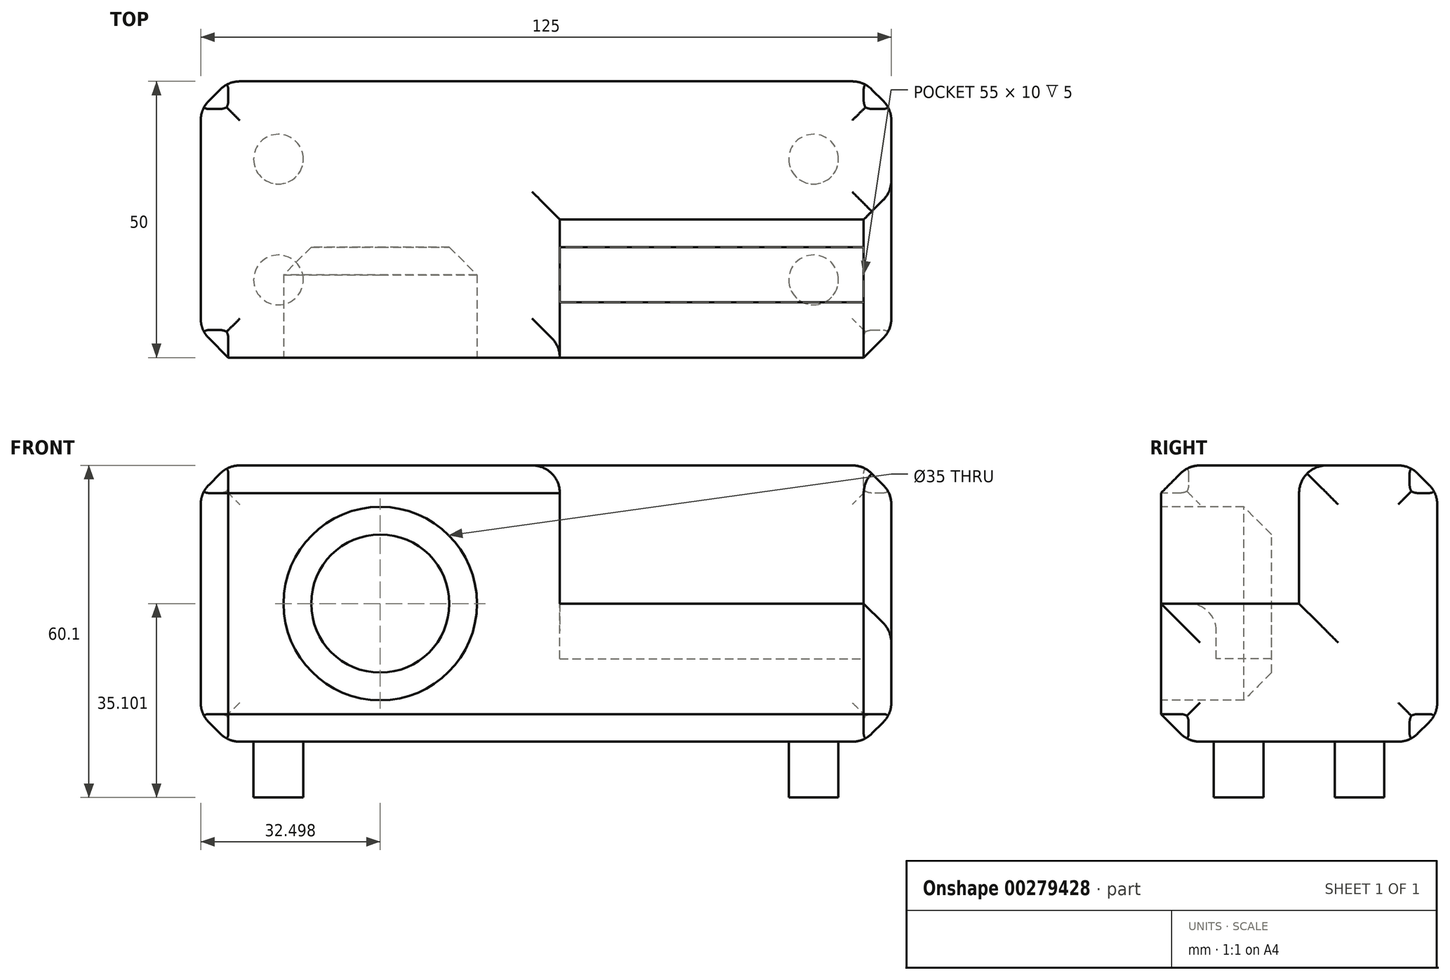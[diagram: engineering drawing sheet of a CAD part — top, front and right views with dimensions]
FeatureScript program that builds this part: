
annotation { "Feature Type Name" : "Feature", "Feature Type Description" : "" }
export const myFeature = defineFeature(function(context is Context, id is Id, definition is map)
    precondition{}
    {
        {
            var Q0;
            Q0=qCreatedBy(makeId("Front.planeOp"),FACE);
            var sketch = newSketch(context, id + "F0", { "sketchPlane" : qUnion([Q0])});
            skLineSegment(sketch, "E0.bottom", {"start": v(-58.26, 27.77) * mm, "end": v(66.74, 27.77) * mm});
            skLineSegment(sketch, "E0.top", {"start": v(-58.26, -22.23) * mm, "end": v(66.74, -22.23) * mm});
            skLineSegment(sketch, "E0.left", {"start": v(-58.26, 27.77) * mm, "end": v(-58.26, -22.23) * mm});
            skLineSegment(sketch, "E0.right", {"start": v(66.74, 27.77) * mm, "end": v(66.74, -22.23) * mm});
            skSolve(sketch);
        }
        {
            var Q0;
            Q0=makeQuery(id+"F0.imprint","IMPRINT",FACE,{"disambiguationData":[TD([[makeQuery(id+"F0.imprint","IMPRINT",EDGE,{"derivedFrom":sQuery(id+"F0.wireOp",EDGE,"E0.bottom")}),-1.0]])]});
            extrude(context, id + "F1", {"entities" : qUnion([Q0]), "depth" : 50 * mm});
        }
        {
            var Q0;
            Q0=makeQuery(id+"F1.opExtrude","CAP_FACE",FACE,{"disambiguationData":[OSD([sQuery(id+"F0.wireOp",EDGE,"E0.bottom"),sQuery(id+"F0.wireOp",EDGE,"E0.top"),sQuery(id+"F0.wireOp",EDGE,"E0.left"),sQuery(id+"F0.wireOp",EDGE,"E0.right")])],"isStart":false});
            var sketch = newSketch(context, id + "F2", { "sketchPlane" : qUnion([Q0])});
            skLineSegment(sketch, "E1.bottom", {"start": v(6.74, 27.77) * mm, "end": v(66.74, 27.77) * mm});
            skLineSegment(sketch, "E1.top", {"start": v(6.74, 2.77) * mm, "end": v(66.74, 2.77) * mm});
            skLineSegment(sketch, "E1.left", {"start": v(6.74, 27.77) * mm, "end": v(6.74, 2.77) * mm});
            skLineSegment(sketch, "E1.right", {"start": v(66.74, 27.77) * mm, "end": v(66.74, 2.77) * mm});
            skSolve(sketch);
        }
        {
            var Q0;
            Q0=qSketchRegion(id+"F2",true);
            extrude(context, id + "F3", {"entities" : qUnion([Q0]), "operationType" : NewBodyOperationType.REMOVE, "oppositeDirection" : true, "depth" : 25 * mm});
        }
        {
            var Q0;
            Q0=makeQuery(id+"F1.opExtrude","CAP_FACE",FACE,{"disambiguationData":[OSD([sQuery(id+"F0.wireOp",EDGE,"E0.bottom"),sQuery(id+"F0.wireOp",EDGE,"E0.top"),sQuery(id+"F0.wireOp",EDGE,"E0.left"),sQuery(id+"F0.wireOp",EDGE,"E0.right")])],"isStart":false});
            var sketch = newSketch(context, id + "F4", { "sketchPlane" : qUnion([Q0])});
            skCircle(sketch, "E2", {"center": v(-25.76, 2.77) * mm, "radius": 17.5 * mm});
            skSolve(sketch);
        }
        {
            var Q0;
            Q0=qSketchRegion(id+"F4",true);
            extrude(context, id + "F5", {"entities" : qUnion([Q0]), "operationType" : NewBodyOperationType.REMOVE, "oppositeDirection" : true, "depth" : 20 * mm});
        }
        {
            var Q0;
            Q0=makeQuery(id+"F1.opExtrude","CAP_EDGE",EDGE,{"disambiguationData":[OSD([sQuery(id+"F0.wireOp",EDGE,"E0.bottom")])],"isStart":false});
            var Q1;
            Q1=makeQuery(id+"F3.boolean.opBoolean","COPY",EDGE,{"derivedFrom":makeQuery(id+"F3.opExtrude","SWEPT_EDGE",EDGE,{"disambiguationData":[OSD([sQuery(id+"F0.wireOp",EDGE,"E0.bottom"),sQuery(id+"F2.wireOp",EDGE,"E1.bottom"),sQuery(id+"F2.wireOp",EDGE,"E1.left")])]})});
            var Q2;
            Q2=makeQuery(id+"F3.boolean.opBoolean","COPY",EDGE,{"derivedFrom":makeQuery(id+"F3.opExtrude","CAP_EDGE",EDGE,{"disambiguationData":[OSD([sQuery(id+"F2.wireOp",EDGE,"E1.bottom")])],"isStart":false})});
            var Q3;
            Q3=makeQuery(id+"F1.opExtrude","SWEPT_EDGE",EDGE,{"disambiguationData":[OSD([sQuery(id+"F0.wireOp",EDGE,"E0.bottom"),sQuery(id+"F0.wireOp",EDGE,"E0.right")])]});
            var Q4;
            Q4=makeQuery(id+"F1.opExtrude","CAP_EDGE",EDGE,{"disambiguationData":[OSD([sQuery(id+"F0.wireOp",EDGE,"E0.bottom")])],"isStart":true});
            var Q5;
            Q5=makeQuery(id+"F1.opExtrude","SWEPT_EDGE",EDGE,{"disambiguationData":[OSD([sQuery(id+"F0.wireOp",EDGE,"E0.bottom"),sQuery(id+"F0.wireOp",EDGE,"E0.left")])]});
            var Q6;
            Q6=makeQuery(id+"F1.opExtrude","CAP_EDGE",EDGE,{"disambiguationData":[OSD([sQuery(id+"F0.wireOp",EDGE,"E0.left")])],"isStart":false});
            var Q7;
            Q7=makeQuery(id+"F5.boolean.opBoolean","COPY",EDGE,{"derivedFrom":makeQuery(id+"F5.opExtrude","CAP_EDGE",EDGE,{"disambiguationData":[OSD([sQuery(id+"F4.wireOp",EDGE,"E2")])],"isStart":true})});
            var Q8;
            Q8=makeQuery(id+"F5.boolean.opBoolean","COPY",EDGE,{"derivedFrom":makeQuery(id+"F5.opExtrude","CAP_EDGE",EDGE,{"disambiguationData":[OSD([sQuery(id+"F4.wireOp",EDGE,"E2")])],"isStart":false})});
            var Q9;
            Q9=makeQuery(id+"F3.boolean.opBoolean","COPY",EDGE,{"derivedFrom":makeQuery(id+"F3.opExtrude","CAP_EDGE",EDGE,{"disambiguationData":[OSD([sQuery(id+"F2.wireOp",EDGE,"E1.top")])],"isStart":true})});
            var Q10;
            Q10=makeQuery(id+"F3.boolean.opBoolean","COPY",EDGE,{"derivedFrom":makeQuery(id+"F3.opExtrude","CAP_EDGE",EDGE,{"disambiguationData":[OSD([sQuery(id+"F2.wireOp",EDGE,"E1.left")])],"isStart":true})});
            var Q11;
            Q11=makeQuery(id+"F3.boolean.opBoolean","COPY",EDGE,{"derivedFrom":makeQuery(id+"F3.opExtrude","CAP_EDGE",EDGE,{"disambiguationData":[OSD([sQuery(id+"F2.wireOp",EDGE,"E1.right")])],"isStart":false})});
            var Q12;
            Q12=makeQuery(id+"F3.boolean.opBoolean","COPY",EDGE,{"derivedFrom":makeQuery(id+"F3.opExtrude","SWEPT_EDGE",EDGE,{"disambiguationData":[OSD([sQuery(id+"F0.wireOp",EDGE,"E0.right"),sQuery(id+"F2.wireOp",EDGE,"E1.top"),sQuery(id+"F2.wireOp",EDGE,"E1.right")])]})});
            var Q13;
            Q13=makeQuery(id+"F1.opExtrude","SWEPT_EDGE",EDGE,{"disambiguationData":[OSD([sQuery(id+"F0.wireOp",EDGE,"E0.top"),sQuery(id+"F0.wireOp",EDGE,"E0.right")])]});
            var Q14;
            Q14=makeQuery(id+"F1.opExtrude","SWEPT_FACE",FACE,{"disambiguationData":[OSD([sQuery(id+"F0.wireOp",EDGE,"E0.right")])]});
            var Q15;
            Q15=makeQuery(id+"F1.opExtrude","CAP_EDGE",EDGE,{"disambiguationData":[OSD([sQuery(id+"F0.wireOp",EDGE,"E0.top")])],"isStart":false});
            var Q16;
            Q16=makeQuery(id+"F1.opExtrude","CAP_EDGE",EDGE,{"disambiguationData":[OSD([sQuery(id+"F0.wireOp",EDGE,"E0.left")])],"isStart":true});
            var Q17;
            Q17=makeQuery(id+"F1.opExtrude","CAP_EDGE",EDGE,{"disambiguationData":[OSD([sQuery(id+"F0.wireOp",EDGE,"E0.top")])],"isStart":true});
            var Q18;
            Q18=makeQuery(id+"F1.opExtrude","SWEPT_EDGE",EDGE,{"disambiguationData":[OSD([sQuery(id+"F0.wireOp",EDGE,"E0.top"),sQuery(id+"F0.wireOp",EDGE,"E0.left")])]});
            chamfer(context, id + "F6", {"entities" : qUnion([Q0, Q1, Q2, Q3, Q4, Q5, Q6, Q7, Q8, Q9, Q10, Q11, Q12, Q13, Q14, Q15, Q16, Q17, Q18]), "width" : 5 * mm, "tangentPropagation" : true});
        }
        {
            var Q0;
            Q0=makeQuery(id+"F3.boolean.opBoolean","COPY",FACE,{"derivedFrom":makeQuery(id+"F3.opExtrude","SWEPT_FACE",FACE,{"disambiguationData":[OSD([sQuery(id+"F2.wireOp",EDGE,"E1.top")])]})});
            var sketch = newSketch(context, id + "F7", { "sketchPlane" : qUnion([Q0])});
            skLineSegment(sketch, "E3.bottom", {"start": v(6.74, -40) * mm, "end": v(61.74, -40) * mm});
            skLineSegment(sketch, "E3.top", {"start": v(6.74, -30) * mm, "end": v(61.74, -30) * mm});
            skLineSegment(sketch, "E3.left", {"start": v(6.74, -40) * mm, "end": v(6.74, -30) * mm});
            skLineSegment(sketch, "E3.right", {"start": v(61.74, -40) * mm, "end": v(61.74, -30) * mm});
            skSolve(sketch);
        }
        {
            var Q0;
            Q0=makeQuery(id+"F7.imprint","IMPRINT",FACE,{"disambiguationData":[TD([[makeQuery(id+"F7.imprint","IMPRINT",EDGE,{"derivedFrom":sQuery(id+"F7.wireOp",EDGE,"E3.bottom")}),1.0]])]});
            extrude(context, id + "F8", {"entities" : qUnion([Q0]), "operationType" : NewBodyOperationType.REMOVE, "oppositeDirection" : true, "depth" : 10 * mm});
        }
        {
            var Q0;
            Q0=makeQuery(id+"F1.opExtrude","SWEPT_FACE",FACE,{"disambiguationData":[OSD([sQuery(id+"F0.wireOp",EDGE,"E0.bottom")])]});
            var Q1;
            Q1=makeQuery(id+"F1.opExtrude","SWEPT_FACE",FACE,{"disambiguationData":[OSD([sQuery(id+"F0.wireOp",EDGE,"E0.top")])]});
            var Q2;
            Q2=makeQuery(id+"F1.opExtrude","CAP_FACE",FACE,{"disambiguationData":[OSD([sQuery(id+"F0.wireOp",EDGE,"E0.bottom"),sQuery(id+"F0.wireOp",EDGE,"E0.top"),sQuery(id+"F0.wireOp",EDGE,"E0.left"),sQuery(id+"F0.wireOp",EDGE,"E0.right")])],"isStart":true});
            var Q3;
            Q3=makeQuery(id+"F1.opExtrude","SWEPT_FACE",FACE,{"disambiguationData":[OSD([sQuery(id+"F0.wireOp",EDGE,"E0.right")])]});
            var Q4;
            Q4=makeQuery(id+"F1.opExtrude","SWEPT_FACE",FACE,{"disambiguationData":[OSD([sQuery(id+"F0.wireOp",EDGE,"E0.left")])]});
            fillet(context, id + "F9", {"entities" : qUnion([Q0, Q1, Q2, Q3, Q4]), "radius" : 5 * mm, "tangentPropagation" : true, "allowEdgeOverflow" : false});
        }
        {
            var Q0;
            Q0=makeQuery(id+"F8.boolean.opBoolean","COPY",EDGE,{"derivedFrom":makeQuery(id+"F8.opExtrude","CAP_EDGE",EDGE,{"disambiguationData":[OSD([sQuery(id+"F7.wireOp",EDGE,"E3.top")])],"isStart":true})});
            var Q1;
            Q1=makeQuery(id+"F8.boolean.opBoolean","COPY",EDGE,{"derivedFrom":makeQuery(id+"F8.opExtrude","CAP_EDGE",EDGE,{"disambiguationData":[OSD([sQuery(id+"F7.wireOp",EDGE,"E3.bottom")])],"isStart":true})});
            fillet(context, id + "F10", {"entities" : qUnion([Q0, Q1]), "radius" : 5 * mm, "tangentPropagation" : true, "allowEdgeOverflow" : false});
        }
        {
            var Q0;
            Q0=makeQuery(id+"F1.opExtrude","SWEPT_FACE",FACE,{"disambiguationData":[OSD([sQuery(id+"F0.wireOp",EDGE,"E0.top")])]});
            var sketch = newSketch(context, id + "F11", { "sketchPlane" : qUnion([Q0])});
            skCircle(sketch, "E4", {"center": v(-44.2, 35.93) * mm, "radius": 4.5 * mm});
            skCircle(sketch, "E5", {"center": v(52.67, 35.93) * mm, "radius": 4.5 * mm});
            skCircle(sketch, "E6", {"center": v(-44.2, 14.07) * mm, "radius": 4.5 * mm});
            skCircle(sketch, "E7", {"center": v(52.67, 14.07) * mm, "radius": 4.5 * mm});
            skSolve(sketch);
        }
        {
            var Q0;
            Q0=makeQuery(id+"F11.imprint","IMPRINT",FACE,{"disambiguationData":[TD([[makeQuery(id+"F11.imprint","IMPRINT",EDGE,{"derivedFrom":sQuery(id+"F11.wireOp",EDGE,"E4")}),1.0]])]});
            var Q1;
            Q1=makeQuery(id+"F11.imprint","IMPRINT",FACE,{"disambiguationData":[TD([[makeQuery(id+"F11.imprint","IMPRINT",EDGE,{"derivedFrom":sQuery(id+"F11.wireOp",EDGE,"E6")}),1.0]])]});
            var Q2;
            Q2=makeQuery(id+"F11.imprint","IMPRINT",FACE,{"disambiguationData":[TD([[makeQuery(id+"F11.imprint","IMPRINT",EDGE,{"derivedFrom":sQuery(id+"F11.wireOp",EDGE,"E7")}),1.0]])]});
            var Q3;
            Q3=makeQuery(id+"F11.imprint","IMPRINT",FACE,{"disambiguationData":[TD([[makeQuery(id+"F11.imprint","IMPRINT",EDGE,{"derivedFrom":sQuery(id+"F11.wireOp",EDGE,"E5")}),1.0]])]});
            extrude(context, id + "F12", {"entities" : qUnion([Q0, Q1, Q2, Q3]), "operationType" : NewBodyOperationType.ADD, "depth" : 10.1 * mm});
        }
    });
